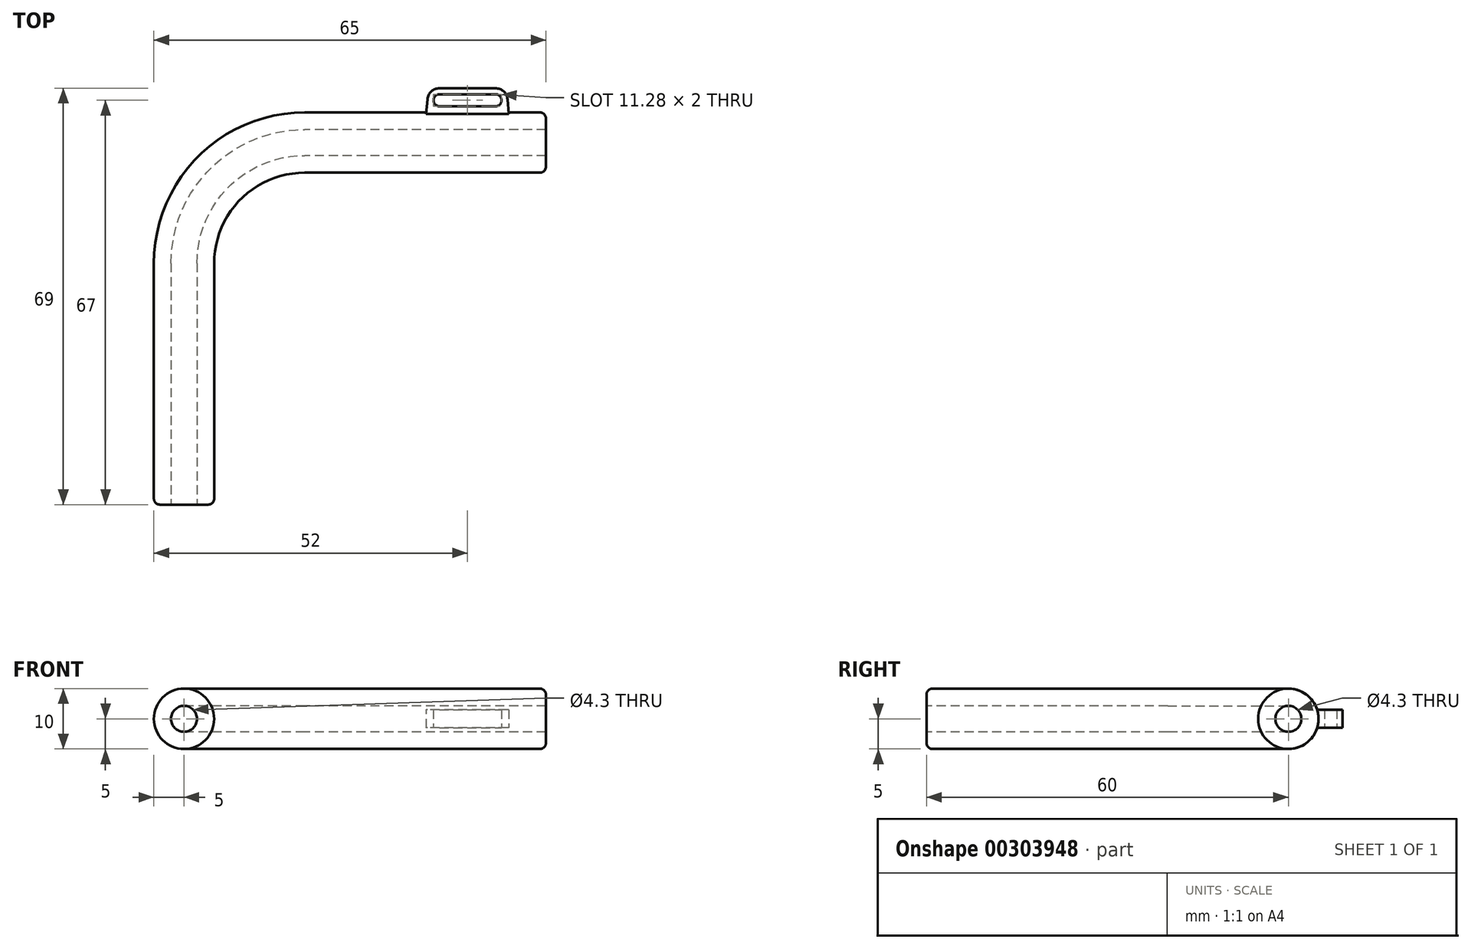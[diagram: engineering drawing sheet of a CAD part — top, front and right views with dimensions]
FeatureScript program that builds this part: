
annotation { "Feature Type Name" : "Feature", "Feature Type Description" : "" }
export const myFeature = defineFeature(function(context is Context, id is Id, definition is map)
    precondition{}
    {
        {
            var Q0;
            Q0=qCreatedBy(makeId("Top.planeOp"),FACE);
            var sketch = newSketch(context, id + "F0", { "sketchPlane" : qUnion([Q0])});
            skLineSegment(sketch, "E0", {"start": v(0, 0) * mm, "end": v(-40, 0) * mm});
            skLineSegment(sketch, "E1", {"start": v(-60, -20) * mm, "end": v(-60, -60) * mm});
            skPoint(sketch, "E2.visualSharp", {"position": v(-60, 0) * mm});
            skArc(sketch, "E2.filletArc", {"start": v(-40, 0) * mm, "mid": v(-54.14, -5.86) * mm, "end": v(-60, -20) * mm});
            skSolve(sketch);
        }
        {
            var Q0;
            Q0=qCreatedBy(makeId("Right.planeOp"),FACE);
            var sketch = newSketch(context, id + "F1", { "sketchPlane" : qUnion([Q0])});
            skCircle(sketch, "E3", {"center": v(0, 0) * mm, "radius": 5 * mm});
            skCircle(sketch, "E4", {"center": v(0, 0) * mm, "radius": 2.15 * mm});
            skSolve(sketch);
        }
        {
            var Q0;
            Q0=makeQuery(id+"F1.imprint","IMPRINT",FACE,{"disambiguationData":[TD([[makeQuery(id+"F1.imprint","IMPRINT",EDGE,{"derivedFrom":sQuery(id+"F1.wireOp",EDGE,"E3")}),1.0]])]});
            var Q1;
            Q1 = qConstructionFilter(qBodyType(qCreatedBy(id + "F0" ,EDGE), BodyType.WIRE), ConstructionObject.NO);
            sweep(context, id + "F2", {"profiles" : qUnion([Q0]), "path" : qUnion([Q1])});
        }
        {
            var Q0;
            Q0=makeQuery(id+"F2.opSweep","CAP_EDGE",EDGE,{"disambiguationData":[OSD([sQuery(id+"F0.wireOp",VERTEX,"E1.end"),sQuery(id+"F1.wireOp",EDGE,"E3")])],"isStart":false});
            var Q1;
            Q1=makeQuery(id+"F2.opSweep","CAP_EDGE",EDGE,{"disambiguationData":[OSD([sQuery(id+"F0.wireOp",VERTEX,"E0.start"),sQuery(id+"F1.wireOp",EDGE,"E3")])],"isStart":true});
            fillet(context, id + "F3", {"entities" : qUnion([Q0, Q1]), "radius" : 1 * mm, "tangentPropagation" : true, "allowEdgeOverflow" : false});
        }
        {
            var Q0;
            Q0=qCreatedBy(makeId("Top.planeOp"),FACE);
            var sketch = newSketch(context, id + "F4", { "sketchPlane" : qUnion([Q0])});
            skLineSegment(sketch, "E5", {"start": v(-20, 3) * mm, "end": v(-6, 3) * mm});
            skLineSegment(sketch, "E6", {"start": v(-6, 3) * mm, "end": v(-6.37, 7.17) * mm});
            skLineSegment(sketch, "E7", {"start": v(-8.36, 9) * mm, "end": v(-17.64, 9) * mm});
            skLineSegment(sketch, "E8", {"start": v(-19.63, 7.17) * mm, "end": v(-20, 3) * mm});
            skPoint(sketch, "E9.visualSharp", {"position": v(-19.48, 9) * mm});
            skArc(sketch, "E9.filletArc", {"start": v(-17.64, 9) * mm, "mid": v(-19, 8.47) * mm, "end": v(-19.63, 7.17) * mm});
            skPoint(sketch, "E10.visualSharp", {"position": v(-6.52, 9) * mm});
            skArc(sketch, "E10.filletArc", {"start": v(-6.37, 7.17) * mm, "mid": v(-7, 8.47) * mm, "end": v(-8.36, 9) * mm});
            skLineSegment(sketch, "E11", {"start": v(-40, 5) * mm, "end": v(-1, 5) * mm});
            skLineSegment(sketch, "E12", {"start": v(-1, -5) * mm, "end": v(-40, -5) * mm});
            skLineSegment(sketch, "E13", {"start": v(-17.64, 7) * mm, "end": v(-8.36, 7) * mm, "construction": true});
            skArc(sketch, "E14.0.startCap", {"start": v(-17.64, 6) * mm, "mid": v(-18.64, 7) * mm, "end": v(-17.64, 8) * mm});
            skArc(sketch, "E14.0.endCap", {"start": v(-8.36, 8) * mm, "mid": v(-7.36, 7) * mm, "end": v(-8.36, 6) * mm});
            skLineSegment(sketch, "E14.0.left", {"start": v(-17.64, 8) * mm, "end": v(-8.36, 8) * mm});
            skLineSegment(sketch, "E14.0.right", {"start": v(-17.64, 6) * mm, "end": v(-8.36, 6) * mm});
            skSolve(sketch);
        }
        {
            var Q0;
            Q0 = qSketchRegion(id + "F4", true);
            extrude(context, id + "F5", {"entities" : qUnion([Q0]), "operationType" : NewBodyOperationType.ADD, "endBound" : BoundingType.SYMMETRIC, "depth" : 3 * mm});
        }
    });
